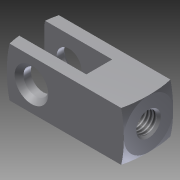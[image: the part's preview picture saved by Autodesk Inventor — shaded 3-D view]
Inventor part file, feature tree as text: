
AUTODESK INVENTOR PART (.ipt)
format: ipt  version: 2012 (Build 160160000, 160)  size: 180,736 bytes
history: native  units: in
note: dims shown in document units (in); Inventor stores cm internally (conversion verified against a paired STEP export)
features: other x126, sketch x7, revolve x3, extrude x2, hole x2
ambient origin geometry x8: Origin, YZ Plane, XZ Plane, XY Plane, X Axis, Y Axis, Z Axis, Center Point
bodies: Solid1 (feature_tree)
feature tree (140):
  extrude  "Extrusion1"  Depth=0.5in TaperAngle=0.0deg
  extrude  "Extrusion2"  TaperAngle=360.0deg  [1 undecoded]
  hole  "Drilling 1"  [1 undecoded]
  hole  "Drilling 2"  [1 undecoded]
  revolve  "Revolution1"  [1 undecoded]
  revolve  "Revolution2"  [1 undecoded]
  revolve  "Revolution3"  [1 undecoded]
  other  "th1_XY"
  other  "th1_YZ"
  other  "th1_ZX"
  other  "th1_X"
  other  "th1_Y"
  other  "th1_Z"
  other  "th1_Center"
  other  "th2_XY"
  other  "th2_YZ"
  other  "th2_ZX"
  other  "th2_X"
  other  "th2_Y"
  other  "th2_Z"
  other  "th2_Center"
  other  "rod_clevis_body_XY"
  other  "rod_clevis_body_YZ"
  other  "rod_clevis_body_ZX"
  other  "rod_clevis_body_X"
  other  "rod_clevis_body_Y"
  other  "rod_clevis_body_Z"
  other  "rod_clevis_body_Center"
  other  "piston_rod_clevis_XY"
  other  "piston_rod_clevis_YZ"
  other  "piston_rod_clevis_ZX"
  other  "piston_rod_clevis_X"
  other  "piston_rod_clevis_Y"
  other  "piston_rod_clevis_Z"
  other  "piston_rod_clevis_Center"
  other  "dummy_XY"
  other  "dummy_YZ"
  other  "dummy_ZX"
  other  "dummy_X"
  other  "dummy_Y"
  other  "dummy_Z"
  other  "dummy_Center"
  other  "l11_XY"
  other  "l11_YZ"
  other  "l11_ZX"
  other  "l11_X"
  other  "l11_Y"
  other  "l11_Z"
  other  "l11_Center"
  other  "l12_XY"
  other  "l12_YZ"
  other  "l12_ZX"
  other  "l12_X"
  other  "l12_Y"
  other  "l12_Z"
  other  "l12_Center"
  other  "l1_XY"
  other  "l1_YZ"
  other  "l1_ZX"
  other  "l1_X"
  other  "l1_Y"
  other  "l1_Z"
  other  "l1_Center"
  other  "h1_XY"
  other  "h1_YZ"
  other  "h1_ZX"
  other  "h1_X"
  other  "h1_Y"
  other  "h1_Z"
  other  "h1_Center"
  other  "l2_XY"
  other  "l2_YZ"
  other  "l2_ZX"
  other  "l2_X"
  other  "l2_Y"
  other  "l2_Z"
  other  "l2_Center"
  other  "h2_XY"
  other  "h2_YZ"
  other  "h2_ZX"
  other  "h2_X"
  other  "h2_Y"
  other  "h2_Z"
  other  "h2_Center"
  other  "w11_XY"
  other  "w11_YZ"
  other  "w11_ZX"
  other  "w11_X"
  other  "w11_Y"
  other  "w11_Z"
  other  "w11_Center"
  other  "w12_XY"
  other  "w12_YZ"
  other  "w12_ZX"
  other  "w12_X"
  other  "w12_Y"
  other  "w12_Z"
  other  "w12_Center"
  other  "l21_XY"
  other  "l21_YZ"
  other  "l21_ZX"
  other  "l21_X"
  other  "l21_Y"
  other  "l21_Z"
  other  "l21_Center"
  other  "l22_XY"
  other  "l22_YZ"
  other  "l22_ZX"
  other  "l22_X"
  other  "l22_Y"
  other  "l22_Z"
  other  "l22_Center"
  other  "w1_XY"
  other  "w1_YZ"
  other  "w1_ZX"
  other  "w1_X"
  other  "w1_Y"
  other  "w1_Z"
  other  "w1_Center"
  other  "w2_XY"
  other  "w2_YZ"
  other  "w2_ZX"
  other  "w2_X"
  other  "w2_Y"
  other  "w2_Z"
  other  "w2_Center"
  other  "to_cylinder_XY"
  other  "to_cylinder_YZ"
  other  "to_cylinder_ZX"
  other  "to_cylinder_X"
  other  "to_cylinder_Y"
  other  "to_cylinder_Z"
  other  "to_cylinder_Center"
  sketch  "Sketch_1"  dims[d0=0.5in d1=0.0in d2=0.5in d3=0.0in]
  sketch  "Sketch_2"  dims[d4=0.211in d5=0.44in d6=0.25in d7=0.25in d8=90.0deg d9=0.44in d10=0.0in]
  sketch  "Sketch3"  dims[d11=0.213in d12=0.75in d13=0.375in d14=0.25in d15=0.5635in d16=0.06in d17=0.0in d18=360.0deg]
  sketch  "Sketch4"  dims[d19=360.0deg d20=360.0deg]
  sketch  "Sketch_5"
  sketch  "Sketch_9"
  sketch  "Sketch_10"
note: 6 required parameter values undecoded (feature->parameter linkage not recoverable at this tier; creation-order binding heuristic only, values carry confidence <= 0.55)
